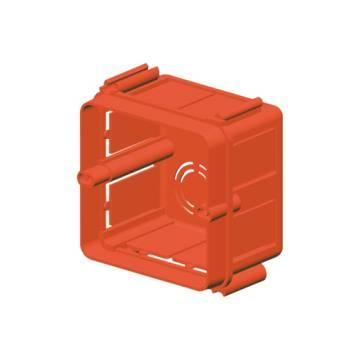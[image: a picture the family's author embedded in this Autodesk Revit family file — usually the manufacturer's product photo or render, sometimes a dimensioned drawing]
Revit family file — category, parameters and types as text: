
# Revit family: Building-ContenitoriIncasso-GEWISS-24SC-SCATOLE-INCASSO_QUADRATA
name_source: partatom
category: Apparecchi elettrici
revit_build: Autodesk Revit 2016 (Build: 20161004_0715(x64)
units: mm (PartAtom-declared; Revit-internal decimal feet)

## family parameters
Condiviso = Sì
Host = Muro
Mantenere orientamento annotazione = Sì
Numero OmniClass = 23.80.30.14.24
Punto di calcolo locali = Sì
Quota connettore circolare = Usa diametro
Sempre verticale = Sì
Taglio con vuoti quando caricato = Sì
Tipo di parte = Normale
Titolo OmniClass = Junction Boxes

## types (1)
- GW24231 - Scatola quadrata 2 posti componibile
    Caratteristiche = Halogen free
    Catalogo = BUILDING
    Catalogo Serie = 24SC
    Codice EAN = 8011564055148
    Codice Electrocod = 0210
    Descrizione = SCATOLA QUADRATA 2 POSTI COMPONIBILE
    Descrizione: = 2 posti componibile
    Dim. esterne BxHxP (mm) = 70x70x50
    Glow Wire Test = 650°C
    IDF = 9ea03b21-96b0-4513-825a-030b5c5d3400
    IDT = c8dd2046-a964-4465-85e7-1ef8ac9c9b0d
    Immagine tipo = GW24231.jpg
    Installazione = Incasso
    Interasse fissaggio supporti = 60MM
    Modello = GW24231
    Per Pareti = Muratura
    Produttore = GEWISS S.p.A.
    SEO = Scatola
    Scheda Tecnica = https://www.gewiss.com
    Temperatura di impiego = -15 +60 °C
    Termopressione con biglia = 70 °C
    URL = https://www.gewiss.com
    Versione file RFA = 19.0
